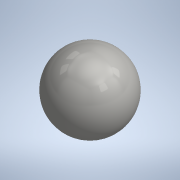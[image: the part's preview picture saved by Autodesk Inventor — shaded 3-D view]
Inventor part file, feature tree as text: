
AUTODESK INVENTOR PART (.ipt)
format: ipt  version: 2022.1 (Build 261234000, 234)  size: 105,472 bytes
history: native  units: mm (DEFAULTED — no unit token found)
features: other x8, revolve x1, sketch x1
bodies: Body1 (feature_tree)
feature tree (10):
  other  "Sólido1"
  other  "Origen"
  revolve  "Revolución1"  [1 undecoded]
  other  "Plano YZ"
  other  "Plano XZ"
  other  "Plano XY"
  other  "Eje X"
  other  "Eje Y"
  other  "Eje Z"
  sketch  "Boceto1"  dims[d0=50.8mm d1=25.4mm d2=90.0deg]
note: 1 required parameter value undecoded (feature->parameter linkage not recoverable at this tier; creation-order binding heuristic only, values carry confidence <= 0.55)
